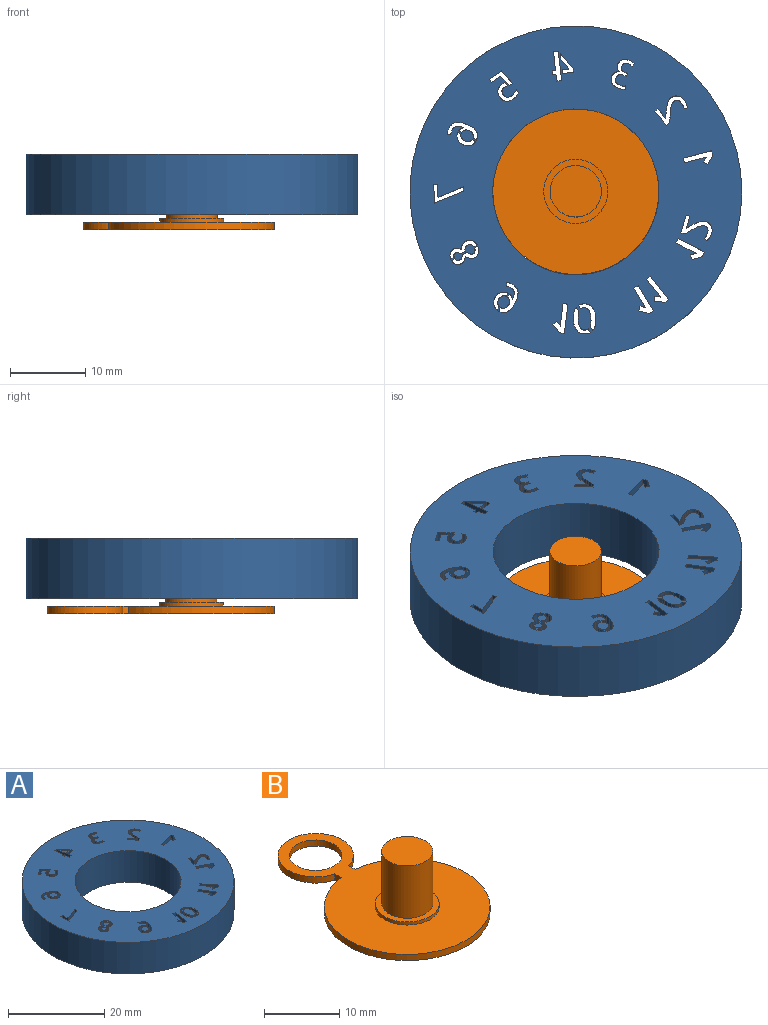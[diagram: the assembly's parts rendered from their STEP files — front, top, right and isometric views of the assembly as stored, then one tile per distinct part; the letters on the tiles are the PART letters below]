
ASSEMBLY  parts=2 mates=1
PART A: 389 faces, bbox 44x44x8 mm
  f0: plane 44x44mm, normal (0,0,1), area 1079.7mm2, adj f2,f3,f4,f5,f6,f7,f8,f9
  f1: plane 44x44mm, normal (0,0,-1), area 1079.7mm2, adj f2,f3,f4,f5,f6,f7,f8,f9
  f2: cylinder r=11mm len=22mm, axis (0,0,-1), area 552.9mm2, adj f0,f1
  f3: cylinder r=22mm len=44mm, axis (0,0,-1), area 1105.8mm2, adj f0,f1
  f4: plane 8x1.21mm, normal (-0.86,0.5,0), area 11.2mm2, adj f0,f1,f5,f10
  f5: plane 8x0.56mm, normal (0.5,0.86,0), area 5.2mm2, adj f0,f1,f4,f6
  f6: plane 8x0.65mm, normal (0.86,-0.5,0), area 6.1mm2, adj f0,f1,f5,f7
  f7: plane 8x2.9mm, normal (-0.25,0.97,0), area 24mm2, adj f0,f1,f6,f8
  f8: plane 8x0.63mm, normal (0.97,0.25,0), area 5.2mm2, adj f0,f1,f7,f9
  f9: plane 8x3.78mm, normal (0.25,-0.97,0), area 31.3mm2, adj f0,f1,f8,f10
  f10: plane 8x0.63mm, normal (-0.97,-0.25,0), area 5.2mm2, adj f0,f1,f4,f9
  f11: plane 8x1.34mm, normal (-0.31,0.95,0), area 11.2mm2, adj f0,f1,f12,f17
  f12: plane 8x0.62mm, normal (0.95,0.3,0), area 5.2mm2, adj f0,f1,f11,f13
  f13: plane 8x0.72mm, normal (0.3,-0.95,0), area 6.1mm2, adj f0,f1,f12,f14
  f14: plane 8x2.66mm, normal (0.46,0.89,0), area 24mm2, adj f0,f1,f13,f15
  f15: plane 8x0.58mm, normal (0.89,-0.46,0), area 5.2mm2, adj f0,f1,f14,f16
  f16: plane 8x3.48mm, normal (-0.46,-0.89,0), area 31.3mm2, adj f0,f1,f15,f17
  f17: plane 8x0.58mm, normal (-0.89,0.46,0), area 5.2mm2, adj f0,f1,f11,f16
  f18: plane 8x0.32mm, normal (0.67,0.74,0), area 3.5mm2, adj f0,f1,f28,f29
  f19: plane 8x0.57mm, normal (0.29,0.96,0), area 4.8mm2, adj f0,f1,f20,f42
  f20: plane 8x2.33mm, normal (0.96,-0.29,0), area 19.4mm2, adj f0,f1,f19,f21
  f21: plane 8x0.49mm, normal (-0.29,-0.96,0), area 4.1mm2, adj f0,f1,f20,f22
  f22: plane 8x1.59mm, normal (-0.96,0.29,0), area 13.3mm2, adj f0,f1,f21,f43
  f23: extruded ~8x0.47mm, area 4mm2, adj f0,f1,f24,f50
  f24: extruded ~8x0.6mm, area 4.8mm2, adj f0,f1,f23,f25
  f25: extruded ~8x0.26mm, area 2.2mm2, adj f0,f1,f24,f26
  f26: extruded ~8x0.27mm, area 2.5mm2, adj f0,f1,f25,f27
  f27: extruded ~8x0.25mm, area 2.5mm2, adj f0,f1,f26,f28
  f28: extruded ~8x0.22mm, area 2.3mm2, adj f0,f1,f18,f27
  f29: extruded ~8x0.14mm, area 1.6mm2, adj f0,f1,f18,f30
  f30: extruded ~8x0.15mm, area 1.5mm2, adj f0,f1,f29,f31
  f31: extruded ~8x0.22mm, area 1.9mm2, adj f0,f1,f30,f32
  f32: extruded ~8x0.32mm, area 2.7mm2, adj f0,f1,f31,f33
  f33: extruded ~8x0.23mm, area 1.8mm2, adj f0,f1,f32,f34
  f34: extruded ~8x0.24mm, area 2mm2, adj f0,f1,f33,f35
  f35: extruded ~8x0.22mm, area 2.1mm2, adj f0,f1,f34,f36
  f36: extruded ~8x0.28mm, area 2.6mm2, adj f0,f1,f35,f37
  f37: extruded ~8x0.4mm, area 3.2mm2, adj f0,f1,f36,f38
  f38: extruded ~8x0.47mm, area 3.9mm2, adj f0,f1,f37,f39
  f39: extruded ~8x0.5mm, area 4.4mm2, adj f0,f1,f38,f40
  f40: extruded ~8x0.48mm, area 4.4mm2, adj f0,f1,f39,f41
  f41: extruded ~8x0.42mm, area 3.9mm2, adj f0,f1,f40,f42
  f42: extruded ~8x0.3mm, area 2.8mm2, adj f0,f1,f19,f41
  f43: extruded ~8x0.31mm, area 2.9mm2, adj f0,f1,f22,f44
  f44: extruded ~8x0.41mm, area 3.7mm2, adj f0,f1,f43,f45
  f45: extruded ~8x0.47mm, area 4.2mm2, adj f0,f1,f44,f46
  f46: extruded ~8x0.49mm, area 4.2mm2, adj f0,f1,f45,f47
  f47: extruded ~8x0.49mm, area 4mm2, adj f0,f1,f46,f48
  f48: extruded ~8x0.44mm, area 3.5mm2, adj f0,f1,f47,f49
  f49: extruded ~8x0.37mm, area 3.3mm2, adj f0,f1,f48,f50
  f50: extruded ~8x0.34mm, area 3.6mm2, adj f0,f1,f23,f49
  f51: plane 8x1.36mm, normal (0.24,0.97,0), area 11.2mm2, adj f0,f1,f52,f57
  f52: plane 8x0.63mm, normal (0.97,-0.24,0), area 5.2mm2, adj f0,f1,f51,f53
  f53: plane 8x0.73mm, normal (-0.24,-0.97,0), area 6.1mm2, adj f0,f1,f52,f54
  f54: plane 8x2.57mm, normal (0.86,0.51,0), area 24mm2, adj f0,f1,f53,f55
  f55: plane 8x0.56mm, normal (0.51,-0.86,0), area 5.2mm2, adj f0,f1,f54,f56
  f56: plane 8x3.36mm, normal (-0.86,-0.51,0), area 31.3mm2, adj f0,f1,f55,f57
  f57: plane 8x0.56mm, normal (-0.51,0.86,0), area 5.2mm2, adj f0,f1,f51,f56
  f58: plane 8x1.39mm, normal (0.11,0.99,0), area 11.2mm2, adj f0,f1,f59,f64
  f59: plane 8x0.64mm, normal (0.99,-0.11,0), area 5.2mm2, adj f0,f1,f58,f60
  f60: plane 8x0.75mm, normal (-0.11,-0.99,0), area 6.1mm2, adj f0,f1,f59,f61
  f61: plane 8x2.34mm, normal (0.78,0.62,0), area 24mm2, adj f0,f1,f60,f62
  f62: plane 8x0.51mm, normal (0.62,-0.78,0), area 5.2mm2, adj f0,f1,f61,f63
  f63: plane 8x3.05mm, normal (-0.78,-0.62,0), area 31.3mm2, adj f0,f1,f62,f64
  f64: plane 8x0.51mm, normal (-0.62,0.78,0), area 5.2mm2, adj f0,f1,f58,f63
  f65: plane 8x0.43mm, normal (-0.84,0.55,0), area 4.1mm2, adj f0,f1,f69,f70
  f66: plane 8x0.4mm, normal (-0.84,0.55,0), area 3.9mm2, adj f0,f1,f77,f78
  f67: extruded ~8x0.45mm, area 4.7mm2, adj f0,f1,f68,f78
  f68: extruded ~8x0.57mm, area 4.8mm2, adj f0,f1,f67,f69
  f69: extruded ~8x0.48mm, area 4.3mm2, adj f0,f1,f65,f68
  f70: extruded ~8x0.3mm, area 3.3mm2, adj f0,f1,f65,f71
  f71: extruded ~8x0.41mm, area 3.6mm2, adj f0,f1,f70,f72
  f72: extruded ~8x0.52mm, area 4.1mm2, adj f0,f1,f71,f73
  f73: extruded ~8x0.6mm, area 5.2mm2, adj f0,f1,f72,f74
  f74: extruded ~8x0.32mm, area 3.6mm2, adj f0,f1,f73,f75
  f75: extruded ~8x0.41mm, area 3.7mm2, adj f0,f1,f74,f76
  f76: extruded ~8x0.47mm, area 3.8mm2, adj f0,f1,f75,f77
  f77: extruded ~8x0.48mm, area 4.1mm2, adj f0,f1,f66,f76
  f78: extruded ~8x0.52mm, area 4.2mm2, adj f0,f1,f66,f67
  f79: plane 8x0.45mm, normal (0.48,-0.88,0), area 4.1mm2, adj f0,f1,f87,f88
  f80: plane 8x0.58mm, normal (0.48,-0.88,0), area 5.3mm2, adj f0,f1,f92,f93
  f81: plane 8x0.44mm, normal (0.48,-0.88,0), area 4mm2, adj f0,f1,f98,f99
  f82: extruded ~8x0.22mm, area 2.1mm2, adj f0,f1,f83,f108
  f83: extruded ~8x0.19mm, area 2mm2, adj f0,f1,f82,f84
  f84: extruded ~8x0.35mm, area 3mm2, adj f0,f1,f83,f85
  f85: extruded ~8x0.36mm, area 2.9mm2, adj f0,f1,f84,f86
  f86: extruded ~8x0.34mm, area 3mm2, adj f0,f1,f85,f87
  f87: extruded ~8x0.35mm, area 3.7mm2, adj f0,f1,f79,f86
  f88: extruded ~8x0.25mm, area 2.7mm2, adj f0,f1,f79,f89
  f89: extruded ~8x0.4mm, area 3.3mm2, adj f0,f1,f88,f90
  f90: extruded ~8x0.29mm, area 3.3mm2, adj f0,f1,f89,f91
  f91: extruded ~8x0.36mm, area 3mm2, adj f0,f1,f90,f92
  f92: extruded ~8x0.06mm, area 0.6mm2, adj f0,f1,f80,f91
  f93: extruded ~8x0.45mm, area 4mm2, adj f0,f1,f80,f94
  f94: extruded ~8x0.41mm, area 3.4mm2, adj f0,f1,f93,f95
  f95: extruded ~8x0.13mm, area 1.5mm2, adj f0,f1,f94,f96
  f96: extruded ~8x0.18mm, area 1.6mm2, adj f0,f1,f95,f97
  f97: extruded ~8x0.21mm, area 1.7mm2, adj f0,f1,f96,f98
  f98: extruded ~8x0.22mm, area 1.8mm2, adj f0,f1,f81,f97
  f99: extruded ~8x0.42mm, area 3.6mm2, adj f0,f1,f81,f100
  f100: extruded ~8x0.42mm, area 3.4mm2, adj f0,f1,f99,f101
  f101: extruded ~8x0.37mm, area 3.3mm2, adj f0,f1,f100,f102
  f102: extruded ~8x0.34mm, area 3.6mm2, adj f0,f1,f101,f103
  f103: extruded ~8x0.31mm, area 2.6mm2, adj f0,f1,f102,f104
  f104: extruded ~8x0.31mm, area 2.5mm2, adj f0,f1,f103,f105
  f105: extruded ~8x0.31mm, area 2.6mm2, adj f0,f1,f104,f106
  f106: extruded ~8x0.3mm, area 2.7mm2, adj f0,f1,f105,f107
  f107: extruded ~8x0.27mm, area 2.2mm2, adj f0,f1,f106,f108
  f108: extruded ~8x0.26mm, area 2.2mm2, adj f0,f1,f82,f107
  f109: plane 8x0.44mm, normal (-0.48,0.88,0), area 4mm2, adj f0,f1,f116,f117
  f110: plane 8x0.08mm, normal (-0.53,-0.85,0), area 0.8mm2, adj f0,f1,f111,f122
  f111: plane 8x0.56mm, normal (-0.48,0.88,0), area 5.1mm2, adj f0,f1,f110,f123
  f112: plane 8x0.45mm, normal (-0.48,0.88,0), area 4.1mm2, adj f0,f1,f126,f127
  f113: extruded ~8x0.61mm, area 5.1mm2, adj f0,f1,f114,f132
  f114: extruded ~8x0.49mm, area 5.6mm2, adj f0,f1,f113,f115
  f115: extruded ~8x0.8mm, area 6.6mm2, adj f0,f1,f114,f116
  f116: extruded ~8x0.67mm, area 7.3mm2, adj f0,f1,f109,f115
  f117: extruded ~8x0.37mm, area 3.6mm2, adj f0,f1,f109,f118
  f118: extruded ~8x0.41mm, area 3.4mm2, adj f0,f1,f117,f119
  f119: extruded ~8x0.21mm, area 2.2mm2, adj f0,f1,f118,f120
  f120: extruded ~8x0.21mm, area 2mm2, adj f0,f1,f119,f121
  f121: extruded ~8x0.21mm, area 1.8mm2, adj f0,f1,f120,f122
  f122: extruded ~8x0.2mm, area 1.6mm2, adj f0,f1,f110,f121
  f123: extruded ~8x0.36mm, area 3.2mm2, adj f0,f1,f111,f124
  f124: extruded ~8x0.29mm, area 2.4mm2, adj f0,f1,f123,f125
  f125: extruded ~8x0.28mm, area 3mm2, adj f0,f1,f124,f126
  f126: extruded ~8x0.37mm, area 3mm2, adj f0,f1,f112,f125
  f127: extruded ~8x0.39mm, area 3.3mm2, adj f0,f1,f112,f128
  f128: extruded ~8x0.37mm, area 3mm2, adj f0,f1,f127,f129
  f129: extruded ~8x0.33mm, area 3mm2, adj f0,f1,f128,f130
  f130: extruded ~8x0.32mm, area 3.4mm2, adj f0,f1,f129,f131
  f131: extruded ~8x0.5mm, area 4.1mm2, adj f0,f1,f130,f132
  f132: extruded ~8x0.51mm, area 4.3mm2, adj f0,f1,f113,f131
  f133: plane 8x2.46mm, normal (1,0.01,0), area 19.7mm2, adj f0,f1,f134,f138
  f134: plane 8x0.52mm, normal (0.01,-1,0), area 4.2mm2, adj f0,f1,f133,f135
  f135: plane 8x1.7mm, normal (-1,-0.01,0), area 13.6mm2, adj f0,f1,f134,f136
  f136: plane 8x3.37mm, normal (0.38,-0.92,0), area 29.2mm2, adj f0,f1,f135,f137
  f137: plane 8x0.59mm, normal (-1,-0.01,0), area 4.8mm2, adj f0,f1,f136,f138
  f138: plane 8x3.89mm, normal (-0.37,0.93,0), area 33.6mm2, adj f0,f1,f133,f137
  f139: plane 8x0.39mm, normal (0.84,-0.55,0), area 3.7mm2, adj f0,f1,f148,f149
  f140: plane 8x0.48mm, normal (0.99,-0.14,0), area 3.9mm2, adj f0,f1,f158,f159
  f141: plane 8x0.44mm, normal (0.84,-0.55,0), area 4.2mm2, adj f0,f1,f168,f169
  f142: extruded ~8x0.28mm, area 2.3mm2, adj f0,f1,f143,f169
  f143: extruded ~8x0.26mm, area 2.4mm2, adj f0,f1,f142,f144
  f144: extruded ~8x0.24mm, area 2.6mm2, adj f0,f1,f143,f145
  f145: extruded ~8x0.29mm, area 2.6mm2, adj f0,f1,f144,f146
  f146: extruded ~8x0.29mm, area 2.3mm2, adj f0,f1,f145,f147
  f147: extruded ~8x0.26mm, area 2.2mm2, adj f0,f1,f146,f148
  f148: extruded ~8x0.22mm, area 2.3mm2, adj f0,f1,f139,f147
  f149: extruded ~8x0.31mm, area 3.2mm2, adj f0,f1,f139,f150
  f150: extruded ~8x0.29mm, area 2.5mm2, adj f0,f1,f149,f151
  f151: extruded ~8x0.02mm, area 0.2mm2, adj f0,f1,f150,f152
  f152: extruded ~8x0.02mm, area 0.2mm2, adj f0,f1,f151,f153
  f153: extruded ~8x0.39mm, area 3.5mm2, adj f0,f1,f152,f154
  f154: extruded ~8x0.39mm, area 3.2mm2, adj f0,f1,f153,f155
  f155: extruded ~8x0.35mm, area 2.9mm2, adj f0,f1,f154,f156
  f156: extruded ~8x0.29mm, area 3.1mm2, adj f0,f1,f155,f157
  f157: extruded ~8x0.36mm, area 3.3mm2, adj f0,f1,f156,f158
  f158: extruded ~8x0.34mm, area 2.8mm2, adj f0,f1,f140,f157
  f159: extruded ~8x0.47mm, area 3.9mm2, adj f0,f1,f140,f160
  f160: extruded ~8x0.49mm, area 4.5mm2, adj f0,f1,f159,f161
  f161: extruded ~8x0.37mm, area 4.1mm2, adj f0,f1,f160,f162
  f162: extruded ~8x0.57mm, area 4.8mm2, adj f0,f1,f161,f163
  f163: extruded ~8x0.8mm, area 6.5mm2, adj f0,f1,f162,f164
  f164: extruded ~8x1.04mm, area 9.4mm2, adj f0,f1,f163,f165
  f165: extruded ~8x0.48mm, area 5mm2, adj f0,f1,f164,f166
  f166: extruded ~8x0.47mm, area 4.4mm2, adj f0,f1,f165,f167
  f167: extruded ~8x0.52mm, area 4.2mm2, adj f0,f1,f166,f168
  f168: extruded ~8x0.55mm, area 4.7mm2, adj f0,f1,f141,f167
  f169: extruded ~8x0.27mm, area 2.3mm2, adj f0,f1,f141,f142
  f170: plane 8x1.1mm, normal (0.79,0.62,0), area 11.2mm2, adj f0,f1,f171,f176
  f171: plane 8x0.51mm, normal (0.62,-0.79,0), area 5.2mm2, adj f0,f1,f170,f172
  f172: plane 8x0.6mm, normal (-0.79,-0.62,0), area 6.1mm2, adj f0,f1,f171,f173
  f173: plane 8x2.98mm, normal (0.99,-0.12,0), area 24mm2, adj f0,f1,f172,f174
  f174: plane 8x0.64mm, normal (-0.12,-0.99,0), area 5.2mm2, adj f0,f1,f173,f175
  f175: plane 8x3.88mm, normal (-0.99,0.12,0), area 31.3mm2, adj f0,f1,f174,f176
  f176: plane 8x0.64mm, normal (0.12,0.99,0), area 5.2mm2, adj f0,f1,f170,f175
  f177: plane 8x0.49mm, normal (0.87,0.49,0), area 4.5mm2, adj f0,f1,f185,f186
  f178: plane 8x0.59mm, normal (0.87,0.49,0), area 5.4mm2, adj f0,f1,f192,f193
  f179: extruded ~8x0.43mm, area 3.5mm2, adj f0,f1,f180,f193
  f180: extruded ~8x0.59mm, area 4.7mm2, adj f0,f1,f179,f181
  f181: extruded ~8x0.69mm, area 5.6mm2, adj f0,f1,f180,f182
  f182: extruded ~8x0.45mm, area 3.9mm2, adj f0,f1,f181,f183
  f183: extruded ~8x0.29mm, area 3mm2, adj f0,f1,f182,f184
  f184: extruded ~8x0.36mm, area 3mm2, adj f0,f1,f183,f185
  f185: extruded ~8x0.4mm, area 3.5mm2, adj f0,f1,f177,f184
  f186: extruded ~8x0.66mm, area 5.5mm2, adj f0,f1,f177,f187
  f187: extruded ~8x0.63mm, area 5.2mm2, adj f0,f1,f186,f188
  f188: extruded ~8x0.5mm, area 4.9mm2, adj f0,f1,f187,f189
  f189: extruded ~8x0.6mm, area 5.6mm2, adj f0,f1,f188,f190
  f190: extruded ~8x0.86mm, area 7mm2, adj f0,f1,f189,f191
  f191: extruded ~8x0.99mm, area 8mm2, adj f0,f1,f190,f192
  f192: extruded ~8x0.68mm, area 6.2mm2, adj f0,f1,f178,f191
  f193: extruded ~8x0.01mm, area 0.1mm2, adj f0,f1,f178,f179
  f194: plane 8x0.6mm, normal (-0.87,-0.49,0), area 5.5mm2, adj f0,f1,f202,f203
  f195: plane 8x0.48mm, normal (-0.87,-0.48,0), area 4.4mm2, adj f0,f1,f196,f209
  f196: extruded ~8x0.63mm, area 5.3mm2, adj f0,f1,f195,f197
  f197: extruded ~8x0.63mm, area 5.1mm2, adj f0,f1,f196,f198
  f198: extruded ~8x0.5mm, area 4.9mm2, adj f0,f1,f197,f199
  f199: extruded ~8x0.6mm, area 5.6mm2, adj f0,f1,f198,f200
  f200: extruded ~8x0.86mm, area 7mm2, adj f0,f1,f199,f201
  f201: extruded ~8x0.98mm, area 7.9mm2, adj f0,f1,f200,f202
  f202: extruded ~8x0.67mm, area 6.1mm2, adj f0,f1,f194,f201
  f203: extruded ~8x0.43mm, area 3.5mm2, adj f0,f1,f194,f204
  f204: extruded ~8x0.57mm, area 4.6mm2, adj f0,f1,f203,f205
  f205: extruded ~8x0.68mm, area 5.6mm2, adj f0,f1,f204,f206
  f206: extruded ~8x0.45mm, area 3.9mm2, adj f0,f1,f205,f207
  f207: extruded ~8x0.29mm, area 3mm2, adj f0,f1,f206,f208
  f208: extruded ~8x0.36mm, area 2.9mm2, adj f0,f1,f207,f209
  f209: extruded ~8x0.38mm, area 3.3mm2, adj f0,f1,f195,f208
  f210: plane 8x0.48mm, normal (0.05,1,0), area 3.9mm2, adj f0,f1,f213,f240
  f211: plane 8x0.46mm, normal (0.46,0.89,0), area 4.2mm2, adj f0,f1,f222,f223
  f212: plane 8x0.41mm, normal (0.46,0.89,0), area 3.7mm2, adj f0,f1,f230,f231
  f213: extruded ~8x0.47mm, area 3.8mm2, adj f0,f1,f210,f214
  f214: extruded ~8x0.51mm, area 4.5mm2, adj f0,f1,f213,f215
  f215: extruded ~8x0.39mm, area 4.1mm2, adj f0,f1,f214,f216
  f216: extruded ~8x0.55mm, area 4.8mm2, adj f0,f1,f215,f217
  f217: extruded ~8x0.81mm, area 6.5mm2, adj f0,f1,f216,f218
  f218: extruded ~8x1.09mm, area 9.4mm2, adj f0,f1,f217,f219
  f219: extruded ~8x0.51mm, area 5mm2, adj f0,f1,f218,f220
  f220: extruded ~8x0.44mm, area 4.4mm2, adj f0,f1,f219,f221
  f221: extruded ~8x0.51mm, area 4.2mm2, adj f0,f1,f220,f222
  f222: extruded ~8x0.57mm, area 4.7mm2, adj f0,f1,f211,f221
  f223: extruded ~8x0.28mm, area 2.3mm2, adj f0,f1,f211,f224
  f224: extruded ~8x0.28mm, area 2.3mm2, adj f0,f1,f223,f225
  f225: extruded ~8x0.25mm, area 2.4mm2, adj f0,f1,f224,f226
  f226: extruded ~8x0.26mm, area 2.6mm2, adj f0,f1,f225,f227
  f227: extruded ~8x0.3mm, area 2.6mm2, adj f0,f1,f226,f228
  f228: extruded ~8x0.29mm, area 2.3mm2, adj f0,f1,f227,f229
  f229: extruded ~8x0.25mm, area 2.2mm2, adj f0,f1,f228,f230
  f230: extruded ~8x0.2mm, area 2.3mm2, adj f0,f1,f212,f229
  f231: extruded ~8x0.29mm, area 3.3mm2, adj f0,f1,f212,f232
  f232: extruded ~8x0.29mm, area 2.5mm2, adj f0,f1,f231,f233
  f233: extruded ~8x0.02mm, area 0.2mm2, adj f0,f1,f232,f234
  f234: extruded ~8x0.02mm, area 0.2mm2, adj f0,f1,f233,f235
  f235: extruded ~8x0.41mm, area 3.5mm2, adj f0,f1,f234,f236
  f236: extruded ~8x0.4mm, area 3.2mm2, adj f0,f1,f235,f237
  f237: extruded ~8x0.35mm, area 3mm2, adj f0,f1,f236,f238
  f238: extruded ~8x0.29mm, area 3.1mm2, adj f0,f1,f237,f239
  f239: extruded ~8x0.38mm, area 3.4mm2, adj f0,f1,f238,f240
  f240: extruded ~8x0.35mm, area 2.8mm2, adj f0,f1,f210,f239
  f241: plane 8x0.46mm, normal (-0.46,-0.89,0), area 4.2mm2, adj f0,f1,f245,f246
  f242: plane 8x0.43mm, normal (-0.46,-0.89,0), area 3.9mm2, adj f0,f1,f253,f254
  f243: extruded ~8x0.41mm, area 4.7mm2, adj f0,f1,f244,f254
  f244: extruded ~8x0.58mm, area 4.8mm2, adj f0,f1,f243,f245
  f245: extruded ~8x0.45mm, area 4.3mm2, adj f0,f1,f241,f244
  f246: extruded ~8x0.3mm, area 3.3mm2, adj f0,f1,f241,f247
  f247: extruded ~8x0.4mm, area 3.7mm2, adj f0,f1,f246,f248
  f248: extruded ~8x0.51mm, area 4.1mm2, adj f0,f1,f247,f249
  f249: extruded ~8x0.62mm, area 5.2mm2, adj f0,f1,f248,f250
  f250: extruded ~8x0.35mm, area 3.6mm2, adj f0,f1,f249,f251
  f251: extruded ~8x0.39mm, area 3.7mm2, adj f0,f1,f250,f252
  f252: extruded ~8x0.46mm, area 3.8mm2, adj f0,f1,f251,f253
  f253: extruded ~8x0.49mm, area 4mm2, adj f0,f1,f242,f252
  f254: extruded ~8x0.52mm, area 4.3mm2, adj f0,f1,f242,f243
  f255: plane 8x0.4mm, normal (-0.75,-0.66,0), area 4.2mm2, adj f0,f1,f257,f280
  f256: plane 8x0.44mm, normal (-0.83,-0.56,0), area 4.2mm2, adj f0,f1,f266,f267
  f257: extruded ~8x0.18mm, area 1.6mm2, adj f0,f1,f255,f258
  f258: extruded ~8x0.17mm, area 1.6mm2, adj f0,f1,f257,f259
  f259: extruded ~8x0.43mm, area 4.4mm2, adj f0,f1,f258,f260
  f260: extruded ~8x0.5mm, area 4.3mm2, adj f0,f1,f259,f261
  f261: extruded ~8x0.53mm, area 5.4mm2, adj f0,f1,f260,f262
  f262: extruded ~8x0.62mm, area 5.3mm2, adj f0,f1,f261,f263
  f263: extruded ~8x0.2mm, area 2.1mm2, adj f0,f1,f262,f264
  f264: extruded ~8x0.22mm, area 2.2mm2, adj f0,f1,f263,f265
  f265: extruded ~8x0.22mm, area 2.1mm2, adj f0,f1,f264,f266
  f266: extruded ~8x0.19mm, area 1.7mm2, adj f0,f1,f256,f265
  f267: extruded ~8x0.15mm, area 1.4mm2, adj f0,f1,f256,f268
  f268: extruded ~8x0.21mm, area 2mm2, adj f0,f1,f267,f269
  f269: extruded ~8x0.23mm, area 2.5mm2, adj f0,f1,f268,f270
  f270: extruded ~8x0.27mm, area 2.8mm2, adj f0,f1,f269,f271
  f271: extruded ~8x0.34mm, area 3.2mm2, adj f0,f1,f270,f272
  f272: extruded ~8x0.46mm, area 3.8mm2, adj f0,f1,f271,f273
  f273: extruded ~8x0.51mm, area 4.3mm2, adj f0,f1,f272,f274
  f274: extruded ~8x0.51mm, area 5.7mm2, adj f0,f1,f273,f275
  f275: extruded ~8x0.4mm, area 3.5mm2, adj f0,f1,f274,f276
  f276: extruded ~8x0.44mm, area 3.5mm2, adj f0,f1,f275,f277
  f277: extruded ~8x0.43mm, area 3.7mm2, adj f0,f1,f276,f278
  f278: extruded ~8x0.36mm, area 4.1mm2, adj f0,f1,f277,f279
  f279: extruded ~8x0.16mm, area 1.5mm2, adj f0,f1,f278,f280
  f280: extruded ~8x0.2mm, area 1.8mm2, adj f0,f1,f255,f279
  f281: plane 8x1.2mm, normal (-0.56,0.83,0), area 11.7mm2, adj f0,f1,f282,f290
  f282: plane 8x0.43mm, normal (0.83,0.56,0), area 4.2mm2, adj f0,f1,f281,f283
  f283: plane 8x1.6mm, normal (0.56,-0.83,0), area 15.5mm2, adj f0,f1,f282,f291
  f284: plane 8x0.41mm, normal (-0.56,0.83,0), area 4mm2, adj f0,f1,f285,f295
  f285: plane 8x0.16mm, normal (0.75,0.66,0), area 1.7mm2, adj f0,f1,f284,f286
  f286: plane 8x0.27mm, normal (0.75,0.66,0), area 2.9mm2, adj f0,f1,f285,f287
  f287: extruded ~8x0.02mm, area 0.2mm2, adj f0,f1,f286,f288
  f288: extruded ~8x0.1mm, area 1mm2, adj f0,f1,f287,f289
  f289: extruded ~8x0.24mm, area 2.6mm2, adj f0,f1,f288,f290
  f290: extruded ~8x0.46mm, area 4.9mm2, adj f0,f1,f281,f289
  f291: extruded ~8x0.76mm, area 8.1mm2, adj f0,f1,f283,f292
  f292: extruded ~8x0.3mm, area 3.1mm2, adj f0,f1,f291,f293
  f293: extruded ~8x0.27mm, area 2.8mm2, adj f0,f1,f292,f294
  f294: extruded ~8x0.22mm, area 2.2mm2, adj f0,f1,f293,f295
  f295: extruded ~8x0.13mm, area 1.3mm2, adj f0,f1,f284,f294
  f296: plane 8x3.89mm, normal (-0.99,-0.11,0), area 31.3mm2, adj f0,f1,f297,f303
  f297: plane 8x0.64mm, normal (-0.11,0.99,0), area 5.2mm2, adj f0,f1,f296,f298
  f298: plane 8x0.91mm, normal (0.99,0.11,0), area 7.3mm2, adj f0,f1,f297,f299
  f299: plane 8x0.41mm, normal (-0.11,0.99,0), area 3.3mm2, adj f0,f1,f298,f300
  f300: plane 8x0.5mm, normal (0.99,0.11,0), area 4mm2, adj f0,f1,f299,f301
  f301: plane 8x0.41mm, normal (0.11,-0.99,0), area 3.3mm2, adj f0,f1,f300,f302
  f302: plane 8x2.48mm, normal (0.99,0.11,0), area 19.9mm2, adj f0,f1,f301,f303
  f303: plane 8x0.64mm, normal (0.11,-0.99,0), area 5.2mm2, adj f0,f1,f296,f302
  f304: plane 8x0.9mm, normal (0.11,-0.99,0), area 7.3mm2, adj f0,f1,f305,f310
  f305: plane 8x1.31mm, normal (0.78,0.63,0), area 13.5mm2, adj f0,f1,f304,f306
  f306: plane 8x0.75mm, normal (0.99,0.11,0), area 6.1mm2, adj f0,f1,f305,f307
  f307: plane 8x2mm, normal (-0.76,-0.65,0), area 21mm2, adj f0,f1,f306,f308
  f308: plane 8x0.5mm, normal (-0.99,-0.11,0), area 4mm2, adj f0,f1,f307,f309
  f309: plane 8x1.47mm, normal (-0.11,0.99,0), area 11.8mm2, adj f0,f1,f308,f310
  f310: plane 8x0.5mm, normal (0.99,0.11,0), area 4mm2, adj f0,f1,f304,f309
  f311: plane 8x0.48mm, normal (-1,0.07,0), area 3.8mm2, adj f0,f1,f323,f324
  f312: plane 8x0.38mm, normal (-0.74,0.68,0), area 4.1mm2, adj f0,f1,f345,f346
  f313: plane 8x0.34mm, normal (-0.37,-0.93,0), area 2.9mm2, adj f0,f1,f314,f355
  f314: plane 8x0.4mm, normal (-0.93,0.38,0), area 3.4mm2, adj f0,f1,f313,f315
  f315: plane 8x0.5mm, normal (0.37,0.93,0), area 4.3mm2, adj f0,f1,f314,f316
  f316: extruded ~8x0.52mm, area 4.3mm2, adj f0,f1,f315,f317
  f317: extruded ~8x0.39mm, area 4.2mm2, adj f0,f1,f316,f318
  f318: extruded ~8x0.53mm, area 4.4mm2, adj f0,f1,f317,f319
  f319: extruded ~8x0.44mm, area 4.8mm2, adj f0,f1,f318,f320
  f320: extruded ~8x0.37mm, area 3.1mm2, adj f0,f1,f319,f321
  f321: extruded ~8x0.23mm, area 1.8mm2, adj f0,f1,f320,f322
  f322: extruded ~8x0.14mm, area 1.1mm2, adj f0,f1,f321,f323
  f323: extruded ~8x0.11mm, area 0.9mm2, adj f0,f1,f311,f322
  f324: extruded ~8x0.38mm, area 3mm2, adj f0,f1,f311,f325
  f325: extruded ~8x0.68mm, area 5.7mm2, adj f0,f1,f324,f326
  f326: extruded ~8x0.16mm, area 1.4mm2, adj f0,f1,f325,f327
  f327: extruded ~8x0.22mm, area 2.1mm2, adj f0,f1,f326,f328
  f328: extruded ~8x0.22mm, area 2.5mm2, adj f0,f1,f327,f329
  f329: extruded ~8x0.29mm, area 2.7mm2, adj f0,f1,f328,f330
  f330: extruded ~8x0.37mm, area 3mm2, adj f0,f1,f329,f331
  f331: extruded ~8x0.45mm, area 3.7mm2, adj f0,f1,f330,f332
  f332: extruded ~8x0.33mm, area 3.2mm2, adj f0,f1,f331,f333
  f333: extruded ~8x0.28mm, area 2.7mm2, adj f0,f1,f332,f334
  f334: extruded ~8x0.29mm, area 2.4mm2, adj f0,f1,f333,f335
  f335: extruded ~8x0.26mm, area 2.1mm2, adj f0,f1,f334,f336
  f336: extruded ~8x0.16mm, area 1.8mm2, adj f0,f1,f335,f337
  f337: extruded ~8x0.23mm, area 2.1mm2, adj f0,f1,f336,f338
  f338: extruded ~8x0.27mm, area 2.2mm2, adj f0,f1,f337,f339
  f339: extruded ~8x0.3mm, area 2.5mm2, adj f0,f1,f338,f340
  f340: extruded ~8x0.42mm, area 4mm2, adj f0,f1,f339,f341
  f341: extruded ~8x0.37mm, area 3.5mm2, adj f0,f1,f340,f342
  f342: extruded ~8x0.43mm, area 3.5mm2, adj f0,f1,f341,f343
  f343: extruded ~8x0.46mm, area 3.8mm2, adj f0,f1,f342,f344
  f344: extruded ~8x0.49mm, area 4.4mm2, adj f0,f1,f343,f345
  f345: extruded ~8x0.26mm, area 2.6mm2, adj f0,f1,f312,f344
  f346: extruded ~8x0.18mm, area 1.9mm2, adj f0,f1,f312,f347
  f347: extruded ~8x0.35mm, area 3.1mm2, adj f0,f1,f346,f348
  f348: extruded ~8x0.38mm, area 3.1mm2, adj f0,f1,f347,f349
  f349: extruded ~8x0.25mm, area 2.1mm2, adj f0,f1,f348,f350
  f350: extruded ~8x0.15mm, area 1.7mm2, adj f0,f1,f349,f351
  f351: extruded ~8x0.18mm, area 1.6mm2, adj f0,f1,f350,f352
  f352: extruded ~8x0.37mm, area 3mm2, adj f0,f1,f351,f353
  f353: extruded ~8x0.23mm, area 2mm2, adj f0,f1,f352,f354
  f354: extruded ~8x0.19mm, area 1.9mm2, adj f0,f1,f353,f355
  f355: extruded ~8x0.22mm, area 1.9mm2, adj f0,f1,f313,f354
  f356: plane 8x0.42mm, normal (-0.27,0.96,0), area 3.5mm2, adj f0,f1,f366,f367
  f357: plane 8x0.45mm, normal (-0.65,0.76,0), area 4.8mm2, adj f0,f1,f358,f380
  f358: plane 8x1.84mm, normal (0.76,0.65,0), area 19.4mm2, adj f0,f1,f357,f359
  f359: plane 8x0.39mm, normal (0.65,-0.76,0), area 4.1mm2, adj f0,f1,f358,f360
  f360: plane 8x1.26mm, normal (-0.76,-0.65,0), area 13.3mm2, adj f0,f1,f359,f381
  f361: extruded ~8x0.48mm, area 4mm2, adj f0,f1,f362,f388
  f362: extruded ~8x0.47mm, area 4.8mm2, adj f0,f1,f361,f363
  f363: extruded ~8x0.22mm, area 2.2mm2, adj f0,f1,f362,f364
  f364: extruded ~8x0.27mm, area 2.5mm2, adj f0,f1,f363,f365
  f365: extruded ~8x0.29mm, area 2.5mm2, adj f0,f1,f364,f366
  f366: extruded ~8x0.28mm, area 2.3mm2, adj f0,f1,f356,f365
  f367: extruded ~8x0.19mm, area 1.6mm2, adj f0,f1,f356,f368
  f368: extruded ~8x0.18mm, area 1.5mm2, adj f0,f1,f367,f369
  f369: extruded ~8x0.2mm, area 1.9mm2, adj f0,f1,f368,f370
  f370: extruded ~8x0.27mm, area 2.7mm2, adj f0,f1,f369,f371
  f371: extruded ~8x0.17mm, area 1.8mm2, adj f0,f1,f370,f372
  f372: extruded ~8x0.23mm, area 2mm2, adj f0,f1,f371,f373
  f373: extruded ~8x0.26mm, area 2.1mm2, adj f0,f1,f372,f374
  f374: extruded ~8x0.28mm, area 2.6mm2, adj f0,f1,f373,f375
  f375: extruded ~8x0.33mm, area 3.2mm2, adj f0,f1,f374,f376
  f376: extruded ~8x0.47mm, area 3.9mm2, adj f0,f1,f375,f377
  f377: extruded ~8x0.54mm, area 4.4mm2, adj f0,f1,f376,f378
  f378: extruded ~8x0.55mm, area 4.4mm2, adj f0,f1,f377,f379
  f379: extruded ~8x0.49mm, area 3.9mm2, adj f0,f1,f378,f380
  f380: extruded ~8x0.35mm, area 2.8mm2, adj f0,f1,f357,f379
  f381: extruded ~8x0.36mm, area 2.9mm2, adj f0,f1,f360,f382
  f382: extruded ~8x0.47mm, area 3.7mm2, adj f0,f1,f381,f383
  f383: extruded ~8x0.52mm, area 4.2mm2, adj f0,f1,f382,f384
  f384: extruded ~8x0.52mm, area 4.2mm2, adj f0,f1,f383,f385
  f385: extruded ~8x0.47mm, area 4mm2, adj f0,f1,f384,f386
  f386: extruded ~8x0.35mm, area 3.5mm2, adj f0,f1,f385,f387
  f387: extruded ~8x0.36mm, area 3.3mm2, adj f0,f1,f386,f388
  f388: extruded ~8x0.45mm, area 3.6mm2, adj f0,f1,f361,f387
PART B: 11 faces, bbox 22x32.9x10 mm
  f0: cylinder r=11mm len=22mm, axis (0,0,-1), area 66.5mm2, adj f1,f2,f5,f6
  f1: plane 32.94x22mm, normal (0,0,1), area 366.2mm2, adj f0,f3,f4,f5,f6,f7
  f2: plane 32.94x22mm, normal (0,0,-1), area 422.9mm2, adj f0,f3,f4,f5,f6
  f3: cylinder r=5mm len=10mm, axis (0,0,-1), area 28.8mm2, adj f1,f2,f5,f6
  f4: cylinder r=3.5mm len=7mm, axis (0,0,-1), area 22mm2, adj f1,f2
  f5: plane 1.2x1mm, normal (-1,0.01,0), area 1.2mm2, adj f0,f1,f2,f3
  f6: plane 1.2x1mm, normal (1,0.01,0), area 1.2mm2, adj f0,f1,f2,f3
  f7: cylinder r=4.25mm len=8.5mm, axis (0,0,-1), area 13.4mm2, adj f1,f8
  f8: plane 8.5x8.5mm, normal (0,0,1), area 20.4mm2, adj f7,f9
  f9: cylinder r=3.4mm len=8.5mm, axis (0,0,-1), area 181.6mm2, adj f8,f10
  f10: plane 6.8x6.8mm, normal (0,0,1), area 36.3mm2, adj f9
PLACE A t=(28.05,7.53,0)mm
PLACE B rot(axis=(0,0,1),32.9deg) t=(28.04,7.62,-2)mm
MATE revolute B.f7 <-> A.f0  axis (0,0,1) through (28.04,7.62,8)mm
